# Revit family: SE
name_source: partatom
category: Lighting Fixtures
revit_build: Autodesk Revit MEP 2012 (Build: 20110916_2132(x64)
units: mm (PartAtom-declared; Revit-internal decimal feet)

## types (4) — shared parameters
Apparent Load = 4 VA
Default Elevation = 48 "
Description = Exit Sign, Die-Cast Aluminum Housing
Glass = Hubbell - light Glass
Lamp = Long-Life LEDs
Load Classification = Lighting
Manufacturer = Dual Lighting
Manufacturer Fax = (866)-898-0131
Model = SE Series
Product Documentation Link = http://www.dual-lite.com
Product Page URL = http://www.dual-lite.com
URL = http://www.dual-lite.com
Voltage = 120 V
Wattage Comments = 2.6 or 3.8 Watts

## per-type parameters (varying)
| type | Finish | Lens |
| SE -  White with Red Exit | Hubbell - Paint - White | Hubbell - Red Glass |
| SE -  White with Green Exit | Hubbell - Paint - White | Hubbell - Green Glass |
| SE -  Black with Red Exit | Hubbell - Paint - Black | Hubbell - Red Glass |
| SE -  Black with Green Exit | Hubbell - Paint - Black | Hubbell - Green Glass |

## geometry (parser evidence)
native form markers: Sweep x5
no freeform markers — native parametric forms only
